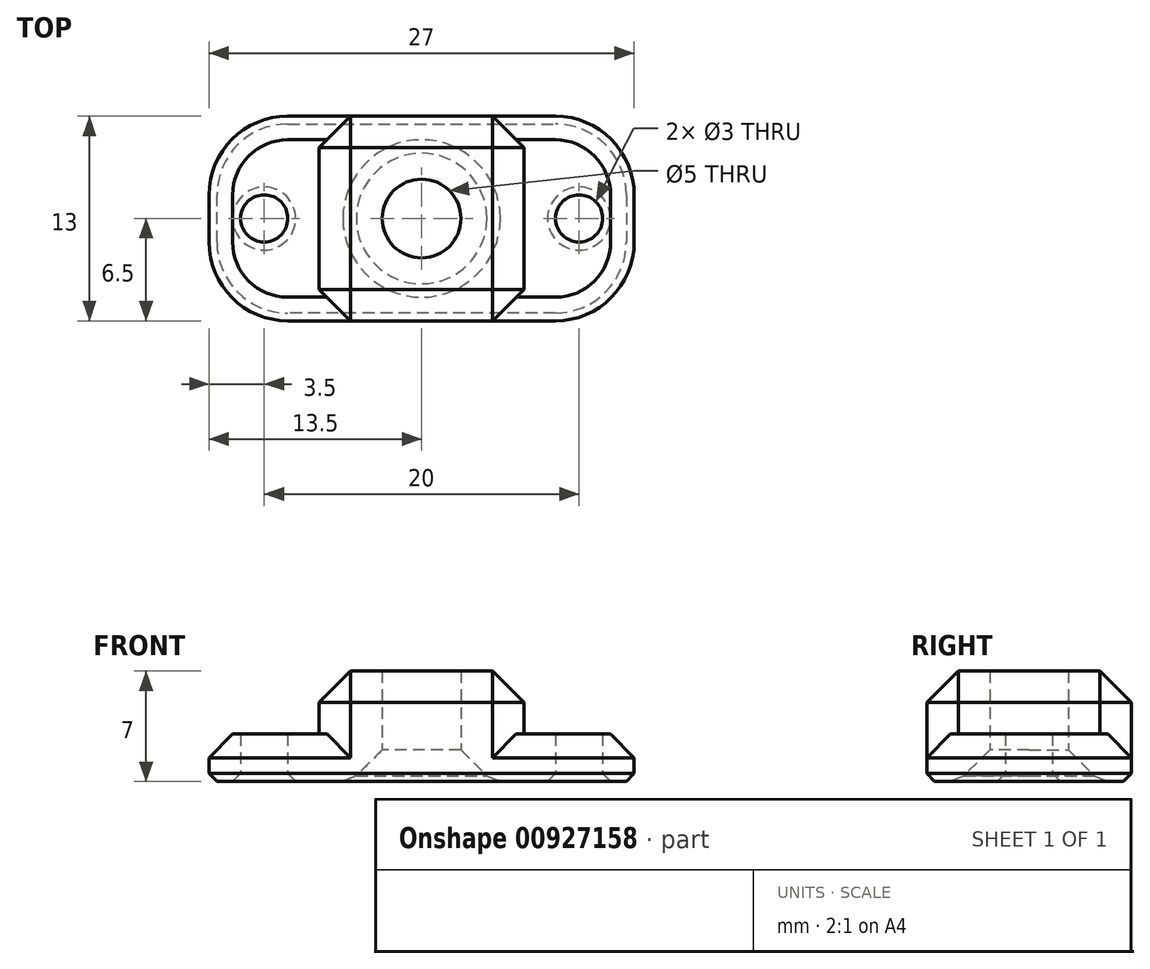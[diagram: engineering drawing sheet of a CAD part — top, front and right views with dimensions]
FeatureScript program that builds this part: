
annotation { "Feature Type Name" : "Feature", "Feature Type Description" : "" }
export const myFeature = defineFeature(function(context is Context, id is Id, definition is map)
    precondition{}
    {
        {
            var Q0;
            Q0=qCreatedBy(makeId("Top.planeOp"),FACE);
            var sketch = newSketch(context, id + "F0", { "sketchPlane" : qUnion([Q0])});
            skCircle(sketch, "E0", {"center": v(0, 0) * mm, "radius": 2.5 * mm});
            skLineSegment(sketch, "E1.bottom", {"start": v(6.5, 6.5) * mm, "end": v(-6.5, 6.5) * mm});
            skLineSegment(sketch, "E1.top", {"start": v(6.5, -6.5) * mm, "end": v(-6.5, -6.5) * mm});
            skLineSegment(sketch, "E1.left", {"start": v(6.5, 6.5) * mm, "end": v(6.5, -6.5) * mm});
            skLineSegment(sketch, "E1.right", {"start": v(-6.5, 6.5) * mm, "end": v(-6.5, -6.5) * mm});
            skCircle(sketch, "E2", {"center": v(0, 0) * mm, "radius": 6.5 * mm, "construction": true});
            skLineSegment(sketch, "E3.bottom", {"start": v(6.5, 6.5) * mm, "end": v(13.5, 6.5) * mm});
            skLineSegment(sketch, "E3.top", {"start": v(6.5, -6.5) * mm, "end": v(13.5, -6.5) * mm});
            skLineSegment(sketch, "E3.right", {"start": v(13.5, 6.5) * mm, "end": v(13.5, -6.5) * mm});
            skLineSegment(sketch, "E4.bottom", {"start": v(-6.5, 6.5) * mm, "end": v(-13.5, 6.5) * mm});
            skLineSegment(sketch, "E4.top", {"start": v(-6.5, -6.5) * mm, "end": v(-13.5, -6.5) * mm});
            skLineSegment(sketch, "E4.right", {"start": v(-13.5, 6.5) * mm, "end": v(-13.5, -6.5) * mm});
            skCircle(sketch, "E5", {"center": v(10, 0) * mm, "radius": 1.5 * mm});
            skPoint(sketch, "E5.centerSnap0", {"position": v(10, 6.5) * mm});
            skCircle(sketch, "E6", {"center": v(-10, 0) * mm, "radius": 1.5 * mm});
            skPoint(sketch, "E6.centerSnap0", {"position": v(-10, 6.5) * mm});
            skPoint(sketch, "E6.centerSnap1", {"position": v(6.5, 0) * mm});
            skSolve(sketch);
        }
        {
            var Q0;
            Q0=makeQuery(id+"F0.imprint","IMPRINT",FACE,{"disambiguationData":[TD([[makeQuery(id+"F0.imprint","IMPRINT",EDGE,{"derivedFrom":sQuery(id+"F0.wireOp",EDGE,"E0")}),-1.0]])]});
            extrude(context, id + "F1", {"entities" : qUnion([Q0]), "depth" : 7 * mm, "offsetDistance" : 25 * mm});
        }
        {
            var Q0;
            Q0=makeQuery(id+"F0.imprint","IMPRINT",FACE,{"disambiguationData":[TD([[makeQuery(id+"F0.imprint","IMPRINT",EDGE,{"derivedFrom":sQuery(id+"F0.wireOp",EDGE,"E4.bottom")}),1.0]])]});
            var Q1;
            Q1=makeQuery(id+"F0.imprint","IMPRINT",FACE,{"disambiguationData":[TD([[makeQuery(id+"F0.imprint","IMPRINT",EDGE,{"derivedFrom":sQuery(id+"F0.wireOp",EDGE,"E3.bottom")}),-1.0]])]});
            extrude(context, id + "F2", {"entities" : qUnion([Q0, Q1]), "operationType" : NewBodyOperationType.ADD, "depth" : 3 * mm, "offsetDistance" : 25 * mm});
        }
        {
            var Q0;
            Q0=makeQuery(id+"F1.opExtrude","CAP_EDGE",EDGE,{"disambiguationData":[OSD([sQuery(id+"F0.wireOp",EDGE,"E0")])],"isStart":true});
            var Q1;
            Q1=makeQuery(id+"F1.opExtrude","CAP_EDGE",EDGE,{"disambiguationData":[OSD([sQuery(id+"F0.wireOp",EDGE,"E1.left")])],"isStart":false});
            var Q2;
            Q2=makeQuery(id+"F1.opExtrude","CAP_EDGE",EDGE,{"disambiguationData":[OSD([sQuery(id+"F0.wireOp",EDGE,"E1.right")])],"isStart":false});
            var Q3;
            Q3=makeQuery(id+"F1.opExtrude","CAP_EDGE",EDGE,{"disambiguationData":[OSD([sQuery(id+"F0.wireOp",EDGE,"E1.top")])],"isStart":false});
            var Q4;
            Q4=makeQuery(id+"F1.opExtrude","CAP_EDGE",EDGE,{"disambiguationData":[OSD([sQuery(id+"F0.wireOp",EDGE,"E1.bottom")])],"isStart":false});
            var Q5;
            Q5=makeQuery(id+"F1.opExtrude","SWEPT_EDGE",EDGE,{"disambiguationData":[OSD([sQuery(id+"F0.wireOp",EDGE,"E1.top"),sQuery(id+"F0.wireOp",EDGE,"E4.top"),sQuery(id+"F0.wireOp",EDGE,"E1.right")])]});
            var Q6;
            Q6=makeQuery(id+"F1.opExtrude","SWEPT_EDGE",EDGE,{"disambiguationData":[OSD([sQuery(id+"F0.wireOp",EDGE,"E1.top"),sQuery(id+"F0.wireOp",EDGE,"E3.top"),sQuery(id+"F0.wireOp",EDGE,"E1.left")])]});
            var Q7;
            Q7=makeQuery(id+"F1.opExtrude","SWEPT_EDGE",EDGE,{"disambiguationData":[OSD([sQuery(id+"F0.wireOp",EDGE,"E1.bottom"),sQuery(id+"F0.wireOp",EDGE,"E4.bottom"),sQuery(id+"F0.wireOp",EDGE,"E1.right")])]});
            var Q8;
            Q8=makeQuery(id+"F1.opExtrude","SWEPT_EDGE",EDGE,{"disambiguationData":[OSD([sQuery(id+"F0.wireOp",EDGE,"E1.bottom"),sQuery(id+"F0.wireOp",EDGE,"E3.bottom"),sQuery(id+"F0.wireOp",EDGE,"E1.left")])]});
            chamfer(context, id + "F3", {"entities" : qUnion([Q0, Q1, Q2, Q3, Q4, Q5, Q6, Q7, Q8]), "width" : 2 * mm, "tangentPropagation" : true});
        }
        {
            var Q0;
            Q0=makeQuery(id+"F2.opExtrude","SWEPT_EDGE",EDGE,{"disambiguationData":[OSD([sQuery(id+"F0.wireOp",EDGE,"E4.bottom"),sQuery(id+"F0.wireOp",EDGE,"E4.right")])]});
            var Q1;
            Q1=makeQuery(id+"F2.opExtrude","SWEPT_EDGE",EDGE,{"disambiguationData":[OSD([sQuery(id+"F0.wireOp",EDGE,"E4.top"),sQuery(id+"F0.wireOp",EDGE,"E4.right")])]});
            var Q2;
            Q2=makeQuery(id+"F2.opExtrude","SWEPT_EDGE",EDGE,{"disambiguationData":[OSD([sQuery(id+"F0.wireOp",EDGE,"E3.top"),sQuery(id+"F0.wireOp",EDGE,"E3.right")])]});
            var Q3;
            Q3=makeQuery(id+"F2.opExtrude","SWEPT_EDGE",EDGE,{"disambiguationData":[OSD([sQuery(id+"F0.wireOp",EDGE,"E3.bottom"),sQuery(id+"F0.wireOp",EDGE,"E3.right")])]});
            fillet(context, id + "F4", {"entities" : qUnion([Q0, Q1, Q2, Q3]), "radius" : 5 * mm, "tangentPropagation" : true, "allowEdgeOverflow" : false});
        }
        {
            var Q0;
            {var subQ0=sQuery(id+"F0.wireOp",EDGE,"E4.right");var subQ1=sQuery(id+"F0.wireOp",EDGE,"E4.top");Q0=makeQuery(id+"F4.opFillet","BLEND_EDGE",EDGE,{"blendedFrom":[makeQuery(id+"F2.opExtrude","SWEPT_EDGE",EDGE,{"disambiguationData":[OSD([subQ1,subQ0])]}),makeQuery(id+"F2.opExtrude","CAP_FACE",FACE,{"disambiguationData":[OSD([sQuery(id+"F0.wireOp",EDGE,"E4.bottom"),subQ1,sQuery(id+"F0.wireOp",EDGE,"E1.right"),subQ0,sQuery(id+"F0.wireOp",EDGE,"E6")])],"isStart":false})],"blendedInto":[makeQuery(id+"F2.opExtrude","CAP_FACE",FACE,{"disambiguationData":[OSD([sQuery(id+"F0.wireOp",EDGE,"E4.bottom"),subQ1,sQuery(id+"F0.wireOp",EDGE,"E1.right"),subQ0,sQuery(id+"F0.wireOp",EDGE,"E6")])],"isStart":false})]});}
            var Q1;
            {var subQ0=sQuery(id+"F0.wireOp",EDGE,"E3.right");var subQ1=sQuery(id+"F0.wireOp",EDGE,"E3.top");Q1=makeQuery(id+"F4.opFillet","BLEND_EDGE",EDGE,{"blendedFrom":[makeQuery(id+"F2.opExtrude","SWEPT_EDGE",EDGE,{"disambiguationData":[OSD([subQ1,subQ0])]}),makeQuery(id+"F2.opExtrude","CAP_FACE",FACE,{"disambiguationData":[OSD([sQuery(id+"F0.wireOp",EDGE,"E3.bottom"),subQ1,sQuery(id+"F0.wireOp",EDGE,"E1.left"),subQ0,sQuery(id+"F0.wireOp",EDGE,"E5")])],"isStart":false})],"blendedInto":[makeQuery(id+"F2.opExtrude","CAP_FACE",FACE,{"disambiguationData":[OSD([sQuery(id+"F0.wireOp",EDGE,"E3.bottom"),subQ1,sQuery(id+"F0.wireOp",EDGE,"E1.left"),subQ0,sQuery(id+"F0.wireOp",EDGE,"E5")])],"isStart":false})]});}
            chamfer(context, id + "F5", {"entities" : qUnion([Q0, Q1]), "width" : 1.5 * mm, "tangentPropagation" : true});
        }
        {
            var Q0;
            {var subQ0=sQuery(id+"F0.wireOp",EDGE,"E1.right");var subQ1=sQuery(id+"F0.wireOp",EDGE,"E1.left");Q0=makeQuery(id+"F2.boolean.opBoolean","MERGE",FACE,{"derivedFrom":[makeQuery(id+"F1.opExtrude","CAP_FACE",FACE,{"disambiguationData":[OSD([sQuery(id+"F0.wireOp",EDGE,"E0"),sQuery(id+"F0.wireOp",EDGE,"E1.bottom"),sQuery(id+"F0.wireOp",EDGE,"E1.top"),subQ1,subQ0])],"isStart":true}),makeQuery(id+"F2.opExtrude","CAP_FACE",FACE,{"disambiguationData":[OSD([sQuery(id+"F0.wireOp",EDGE,"E3.bottom"),sQuery(id+"F0.wireOp",EDGE,"E3.top"),subQ1,sQuery(id+"F0.wireOp",EDGE,"E3.right"),sQuery(id+"F0.wireOp",EDGE,"E5")])],"isStart":true}),makeQuery(id+"F2.opExtrude","CAP_FACE",FACE,{"disambiguationData":[OSD([sQuery(id+"F0.wireOp",EDGE,"E4.bottom"),sQuery(id+"F0.wireOp",EDGE,"E4.top"),subQ0,sQuery(id+"F0.wireOp",EDGE,"E4.right"),sQuery(id+"F0.wireOp",EDGE,"E6")])],"isStart":true})]});}
            chamfer(context, id + "F6", {"entities" : qUnion([Q0]), "width" : 0.5 * mm, "tangentPropagation" : true});
        }
    });
